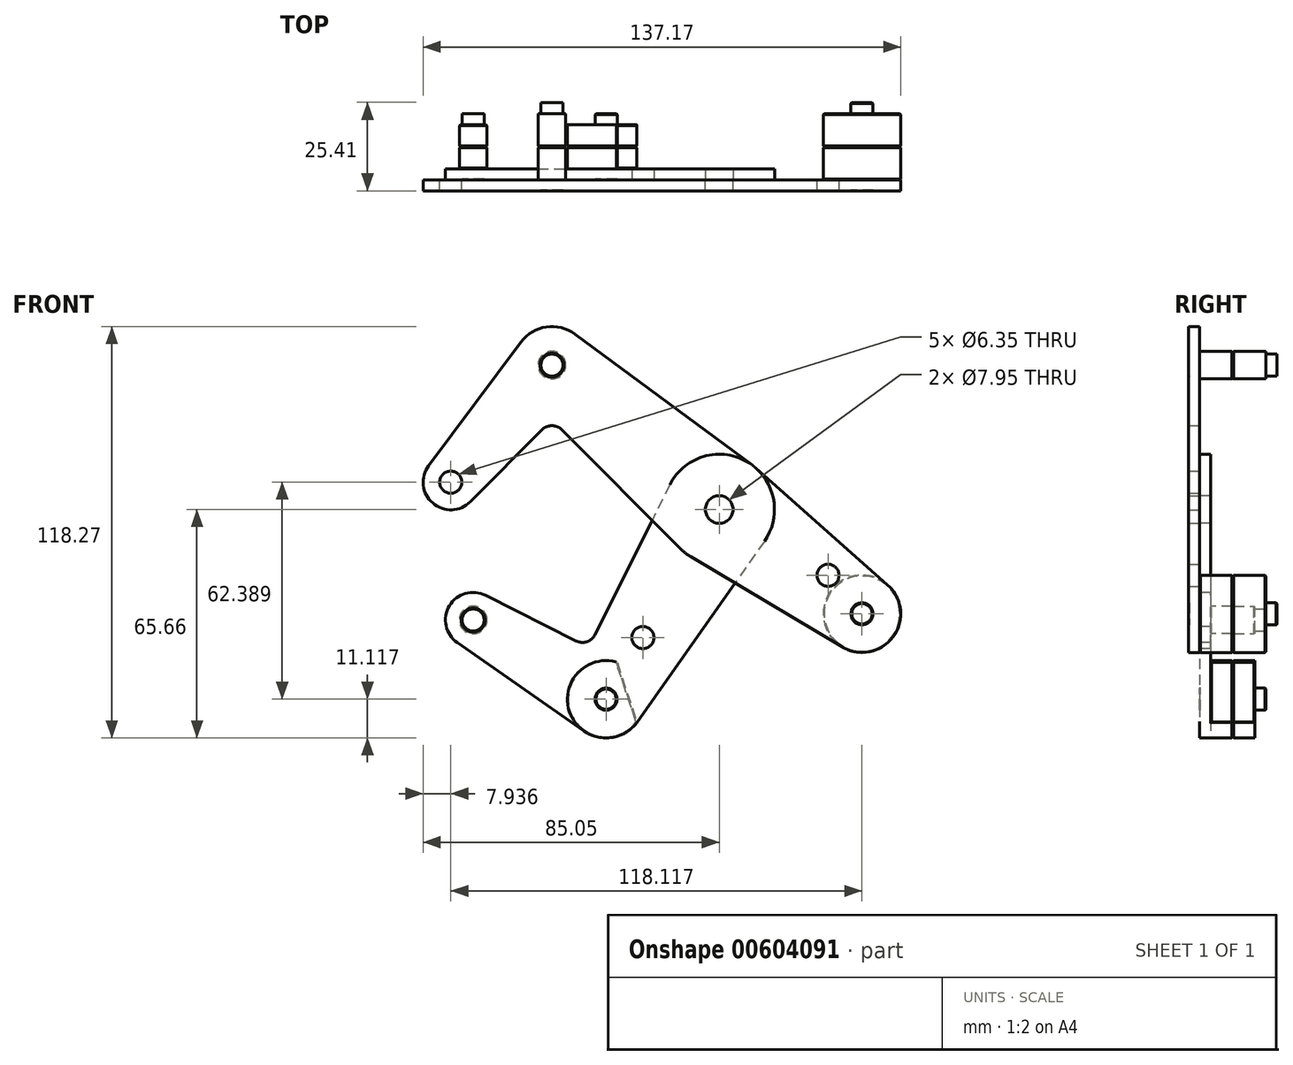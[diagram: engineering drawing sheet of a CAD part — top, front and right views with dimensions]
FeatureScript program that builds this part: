
annotation { "Feature Type Name" : "Feature", "Feature Type Description" : "" }
export const myFeature = defineFeature(function(context is Context, id is Id, definition is map)
    precondition{}
    {
        {
            var Q0;
            Q0=qCreatedBy(makeId("Front.planeOp"),FACE);
            var sketch = newSketch(context, id + "F0", { "sketchPlane" : qUnion([Q0])});
            skCircle(sketch, "E0", {"center": v(0, 0) * mm, "radius": 3.98 * mm});
            skCircle(sketch, "E1", {"center": v(0, 0) * mm, "radius": 15.88 * mm});
            skLineSegment(sketch, "E2", {"start": v(0, 0) * mm, "end": v(-48.07, 41.5) * mm, "construction": true});
            skLineSegment(sketch, "E3", {"start": v(-48.07, 41.5) * mm, "end": v(-77.11, 7.85) * mm, "construction": true});
            skCircle(sketch, "E4", {"center": v(-48.07, 41.5) * mm, "radius": 3.18 * mm});
            skCircle(sketch, "E5", {"center": v(-48.07, 41.5) * mm, "radius": 11.11 * mm});
            skCircle(sketch, "E6", {"center": v(-77.11, 7.85) * mm, "radius": 3.18 * mm});
            skCircle(sketch, "E7", {"center": v(-77.11, 7.85) * mm, "radius": 7.94 * mm});
            skLineSegment(sketch, "E8", {"start": v(0, 0) * mm, "end": v(41, -29.99) * mm, "construction": true});
            skCircle(sketch, "E9", {"center": v(41, -29.99) * mm, "radius": 3.18 * mm});
            skCircle(sketch, "E10", {"center": v(41, -29.99) * mm, "radius": 11.11 * mm});
            skCircle(sketch, "E11", {"center": v(31.24, -18.92) * mm, "radius": 3.18 * mm});
            skLineSegment(sketch, "E12", {"start": v(-83.48, 12.59) * mm, "end": v(-56.98, 48.14) * mm});
            skArc(sketch, "E13", {"start": v(-45.25, 22.92) * mm, "mid": v(-48.07, 24.1) * mm, "end": v(-50.88, 22.92) * mm});
            skLineSegment(sketch, "E14", {"start": v(-71.5, 2.24) * mm, "end": v(-50.88, 22.92) * mm});
            skLineSegment(sketch, "E15", {"start": v(-41.46, 50.43) * mm, "end": v(9.44, 12.76) * mm});
            skLineSegment(sketch, "E16", {"start": v(-45.25, 22.92) * mm, "end": v(-11.25, -11.2) * mm});
            skLineSegment(sketch, "E17", {"start": v(-8.13, -13.64) * mm, "end": v(35.31, -39.53) * mm});
            skLineSegment(sketch, "E18", {"start": v(10.53, 11.88) * mm, "end": v(48.38, -21.67) * mm});
            skLineSegment(sketch, "E19", {"start": v(0, 0) * mm, "end": v(-32.52, -54.54) * mm, "construction": true});
            skLineSegment(sketch, "E20", {"start": v(-32.52, -54.54) * mm, "end": v(-70.7, -31.78) * mm, "construction": true});
            skCircle(sketch, "E21", {"center": v(-32.52, -54.54) * mm, "radius": 3.18 * mm});
            skCircle(sketch, "E22", {"center": v(-32.52, -54.54) * mm, "radius": 11.11 * mm});
            skCircle(sketch, "E23", {"center": v(-70.7, -31.78) * mm, "radius": 3.18 * mm});
            skCircle(sketch, "E24", {"center": v(-70.7, -31.78) * mm, "radius": 7.94 * mm});
            skCircle(sketch, "E25", {"center": v(-21.94, -36.8) * mm, "radius": 3.18 * mm});
            skArc(sketch, "E26", {"start": v(-41.05, -37.81) * mm, "mid": v(-38, -38.03) * mm, "end": v(-35.7, -36.03) * mm});
            skLineSegment(sketch, "E27", {"start": v(12.99, -9.13) * mm, "end": v(-23.42, -60.93) * mm});
            skLineSegment(sketch, "E28", {"start": v(-14.2, 7.08) * mm, "end": v(-35.7, -36.03) * mm});
            skLineSegment(sketch, "E29", {"start": v(-67.13, -24.7) * mm, "end": v(-41.05, -37.81) * mm});
            skLineSegment(sketch, "E30", {"start": v(-75.24, -38.3) * mm, "end": v(-38.87, -63.66) * mm});
            skCircle(sketch, "E31", {"center": v(0, 0) * mm, "radius": 3.18 * mm});
            skSolve(sketch);
        }
        {
            var Q0;
            Q0=makeQuery(id+"F0.imprint","IMPRINT",FACE,{"disambiguationData":[TD([[makeQuery(id+"F0.imprint","IMPRINT",EDGE,{"derivedFrom":sQuery(id+"F0.wireOp",EDGE,"E4")}),-1.0]])]});
            var Q1;
            Q1=makeQuery(id+"F0.imprint","IMPRINT",FACE,{"disambiguationData":[TD([[makeQuery(id+"F0.imprint","IMPRINT",EDGE,{"derivedFrom":sQuery(id+"F0.wireOp",EDGE,"E6")}),-1.0]])]});
            var Q2;
            Q2=makeQuery(id+"F0.imprint","IMPRINT",FACE,{"disambiguationData":[TD([[makeQuery(id+"F0.imprint","IMPRINT",EDGE,{"derivedFrom":sQuery(id+"F0.wireOp",EDGE,"E9")}),-1.0]])]});
            var Q3;
            {var subQ0=sQuery(id+"F0.wireOp",EDGE,"E16");var subQ1=sQuery(id+"F0.wireOp",EDGE,"E1");var subQ2=makeQuery(id+"F0.imprint","INTERSECT",VERTEX,{"derivedFrom":[subQ1,subQ0]});Q3=makeQuery(id+"F0.imprint","IMPRINT",FACE,{"disambiguationData":[TD([[makeQuery(id+"F0.imprint","IMPRINT",EDGE,{"disambiguationData":[TD([[subQ2,1.0]])],"derivedFrom":subQ1}),-1.0]])]});}
            var Q4;
            {var subQ0=sQuery(id+"F0.wireOp",EDGE,"E17");var subQ1=sQuery(id+"F0.wireOp",EDGE,"E1");var subQ2=makeQuery(id+"F0.imprint","INTERSECT",VERTEX,{"derivedFrom":[subQ1,subQ0]});Q4=makeQuery(id+"F0.imprint","IMPRINT",FACE,{"disambiguationData":[TD([[makeQuery(id+"F0.imprint","IMPRINT",EDGE,{"disambiguationData":[TD([[subQ2,-1.0]])],"derivedFrom":subQ1}),-1.0]])]});}
            var Q5;
            {var subQ0=sQuery(id+"F0.wireOp",EDGE,"E12");Q5=makeQuery(id+"F0.imprint","IMPRINT",FACE,{"disambiguationData":[TD([[makeQuery(id+"F0.imprint","IMPRINT",EDGE,{"derivedFrom":subQ0}),-1.0]])]});}
            var Q6;
            Q6=makeQuery(id+"F0.imprint","IMPRINT",FACE,{"disambiguationData":[TD([[makeQuery(id+"F0.imprint","IMPRINT",EDGE,{"derivedFrom":sQuery(id+"F0.wireOp",EDGE,"E11")}),-1.0]])]});
            var Q7;
            Q7=makeQuery(id+"F0.imprint","IMPRINT",FACE,{"disambiguationData":[TD([[makeQuery(id+"F0.imprint","IMPRINT",EDGE,{"derivedFrom":sQuery(id+"F0.wireOp",EDGE,"E0")}),-1.0]])]});
            extrude(context, id + "F1", {"entities" : qUnion([Q0, Q1, Q2, Q3, Q4, Q5, Q6, Q7]), "depth" : 3.17 * mm, "offsetDistance" : 25.4 * mm});
        }
        {
            var Q0;
            Q0=makeQuery(id+"F0.imprint","IMPRINT",FACE,{"disambiguationData":[TD([[makeQuery(id+"F0.imprint","IMPRINT",EDGE,{"derivedFrom":sQuery(id+"F0.wireOp",EDGE,"E25")}),-1.0]])]});
            var Q1;
            Q1=makeQuery(id+"F0.imprint","IMPRINT",FACE,{"disambiguationData":[TD([[makeQuery(id+"F0.imprint","IMPRINT",EDGE,{"derivedFrom":sQuery(id+"F0.wireOp",EDGE,"E0")}),-1.0]])]});
            var Q2;
            {var subQ0=sQuery(id+"F0.wireOp",EDGE,"E17");var subQ1=sQuery(id+"F0.wireOp",EDGE,"E1");var subQ2=makeQuery(id+"F0.imprint","INTERSECT",VERTEX,{"derivedFrom":[subQ1,subQ0]});Q2=makeQuery(id+"F0.imprint","IMPRINT",FACE,{"disambiguationData":[TD([[makeQuery(id+"F0.imprint","IMPRINT",EDGE,{"disambiguationData":[TD([[subQ2,-1.0]])],"derivedFrom":subQ1}),-1.0]])]});}
            var Q3;
            {var subQ0=sQuery(id+"F0.wireOp",EDGE,"E16");var subQ1=sQuery(id+"F0.wireOp",EDGE,"E1");var subQ2=makeQuery(id+"F0.imprint","INTERSECT",VERTEX,{"derivedFrom":[subQ1,subQ0]});Q3=makeQuery(id+"F0.imprint","IMPRINT",FACE,{"disambiguationData":[TD([[makeQuery(id+"F0.imprint","IMPRINT",EDGE,{"disambiguationData":[TD([[subQ2,1.0]])],"derivedFrom":subQ1}),-1.0]])]});}
            var Q4;
            Q4=makeQuery(id+"F0.imprint","IMPRINT",FACE,{"disambiguationData":[TD([[makeQuery(id+"F0.imprint","IMPRINT",EDGE,{"derivedFrom":sQuery(id+"F0.wireOp",EDGE,"E23")}),-1.0]])]});
            var Q5;
            Q5=makeQuery(id+"F0.imprint","IMPRINT",FACE,{"disambiguationData":[TD([[makeQuery(id+"F0.imprint","IMPRINT",EDGE,{"derivedFrom":sQuery(id+"F0.wireOp",EDGE,"E21")}),-1.0]])]});
            extrude(context, id + "F2", {"entities" : qUnion([Q0, Q1, Q2, Q3, Q4, Q5]), "oppositeDirection" : true, "depth" : 3.17 * mm, "offsetDistance" : 25.4 * mm});
        }
        {
            var Q0;
            Q0=makeQuery(id+"F1.opExtrude","CAP_FACE",FACE,{"disambiguationData":[OSD([sQuery(id+"F0.wireOp",EDGE,"E0"),sQuery(id+"F0.wireOp",EDGE,"E1"),sQuery(id+"F0.wireOp",EDGE,"E4"),sQuery(id+"F0.wireOp",EDGE,"E5"),sQuery(id+"F0.wireOp",EDGE,"E6"),sQuery(id+"F0.wireOp",EDGE,"E7"),sQuery(id+"F0.wireOp",EDGE,"E9"),sQuery(id+"F0.wireOp",EDGE,"E10"),sQuery(id+"F0.wireOp",EDGE,"E11"),sQuery(id+"F0.wireOp",EDGE,"E12"),sQuery(id+"F0.wireOp",EDGE,"E13"),sQuery(id+"F0.wireOp",EDGE,"E14"),sQuery(id+"F0.wireOp",EDGE,"E15"),sQuery(id+"F0.wireOp",EDGE,"E16"),sQuery(id+"F0.wireOp",EDGE,"E17"),sQuery(id+"F0.wireOp",EDGE,"E18")])],"isStart":false});
            var sketch = newSketch(context, id + "F3", { "sketchPlane" : qUnion([Q0])});
            skCircle(sketch, "E32", {"center": v(41, -29.99) * mm, "radius": 11.11 * mm});
            skCircle(sketch, "E33", {"center": v(0, 0) * mm, "radius": 3.98 * mm});
            skCircle(sketch, "E34", {"center": v(-48.07, 41.5) * mm, "radius": 3.98 * mm});
            skSolve(sketch);
        }
        {
            var Q0;
            Q0=makeQuery(id+"F0.imprint","IMPRINT",FACE,{"disambiguationData":[TD([[makeQuery(id+"F0.imprint","IMPRINT",EDGE,{"derivedFrom":sQuery(id+"F0.wireOp",EDGE,"E25")}),-1.0]])]});
            var sketch = newSketch(context, id + "F4", { "sketchPlane" : qUnion([Q0])});
            skCircle(sketch, "E35", {"center": v(-32.52, -54.54) * mm, "radius": 11.11 * mm});
            skCircle(sketch, "E36", {"center": v(-70.7, -31.78) * mm, "radius": 3.98 * mm});
            skLineSegment(sketch, "E37", {"start": v(-29.38, -43.88) * mm, "end": v(-23.6, -61.18) * mm});
            skLineSegment(sketch, "E38", {"start": v(-26.5, -52.53) * mm, "end": v(41, -29.99) * mm, "construction": true});
            skSolve(sketch);
        }
        {
            var Q0;
            Q0=qCreatedBy(makeId("Front.planeOp"),FACE);
            cPlane(context, id + "F5", {"entities" : qUnion([Q0]), "cplaneType" : CPlaneType.OFFSET, "offset" : 9.52 * mm, "oppositeDirection" : true, "width" : 152.4 * mm, "height" : 152.4 * mm});
        }
        {
            var Q0;
            {var subQ2=sQuery(id+"F4.wireOp",EDGE,"E37");Q0=makeQuery(id+"F4.imprint","IMPRINT",FACE,{"disambiguationData":[TD([[makeQuery(id+"F4.imprint","IMPRINT",EDGE,{"derivedFrom":subQ2}),-1.0]])]});}
            var Q1;
            Q1=makeQuery(id+"F3.imprint","IMPRINT",FACE,{"disambiguationData":[TD([[makeQuery(id+"F3.imprint","IMPRINT",EDGE,{"derivedFrom":makeQuery(id+"F1.opExtrude","CAP_EDGE",EDGE,{"disambiguationData":[OSD([sQuery(id+"F0.wireOp",EDGE,"E9")])],"isStart":false})}),1.0]])]});
            var Q2;
            Q2=makeQuery(id+"F3.imprint","IMPRINT",FACE,{"disambiguationData":[TD([[makeQuery(id+"F3.imprint","IMPRINT",EDGE,{"derivedFrom":makeQuery(id+"F1.opExtrude","CAP_EDGE",EDGE,{"disambiguationData":[OSD([sQuery(id+"F0.wireOp",EDGE,"E9")])],"isStart":false})}),-1.0]])]});
            var Q3;
            Q3=makeQuery(id+"F3.imprint","IMPRINT",FACE,{"disambiguationData":[TD([[makeQuery(id+"F3.imprint","IMPRINT",EDGE,{"derivedFrom":makeQuery(id+"F1.opExtrude","CAP_EDGE",EDGE,{"disambiguationData":[OSD([sQuery(id+"F0.wireOp",EDGE,"E4")])],"isStart":false})}),1.0]])]});
            var Q4;
            Q4=makeQuery(id+"F4.imprint","IMPRINT",FACE,{"disambiguationData":[TD([[makeQuery(id+"F4.imprint","IMPRINT",EDGE,{"derivedFrom":sQuery(id+"F4.wireOp",EDGE,"E36")}),1.0]])]});
            var Q5;
            Q5=makeQuery(id+"F3.imprint","IMPRINT",FACE,{"disambiguationData":[TD([[makeQuery(id+"F3.imprint","IMPRINT",EDGE,{"derivedFrom":sQuery(id+"F3.wireOp",EDGE,"E34")}),1.0]])]});
            var Q6;
            Q6=qCreatedBy(id+"F5.planeOp",FACE);
            extrude(context, id + "F6", {"entities" : qUnion([Q0, Q1, Q2, Q3, Q4, Q5]), "endBound" : BoundingType.UP_TO_SURFACE, "oppositeDirection" : true, "depth" : 25.4 * mm, "endBoundEntityFace" : qUnion([Q6]), "offsetDistance" : 25.4 * mm});
        }
        {
            var Q0;
            Q0=makeQuery(id+"F1.opExtrude","SWEPT_BODY",BODY,{"disambiguationData":[OSD([sQuery(id+"F0.wireOp",EDGE,"E0"),sQuery(id+"F0.wireOp",EDGE,"E1"),sQuery(id+"F0.wireOp",EDGE,"E4"),sQuery(id+"F0.wireOp",EDGE,"E5"),sQuery(id+"F0.wireOp",EDGE,"E6"),sQuery(id+"F0.wireOp",EDGE,"E7"),sQuery(id+"F0.wireOp",EDGE,"E9"),sQuery(id+"F0.wireOp",EDGE,"E10"),sQuery(id+"F0.wireOp",EDGE,"E11"),sQuery(id+"F0.wireOp",EDGE,"E12"),sQuery(id+"F0.wireOp",EDGE,"E13"),sQuery(id+"F0.wireOp",EDGE,"E14"),sQuery(id+"F0.wireOp",EDGE,"E15"),sQuery(id+"F0.wireOp",EDGE,"E16"),sQuery(id+"F0.wireOp",EDGE,"E17"),sQuery(id+"F0.wireOp",EDGE,"E18")])]});
            var Q1;
            Q1=makeQuery(id+"F2.opExtrude","SWEPT_BODY",BODY,{"disambiguationData":[OSD([sQuery(id+"F0.wireOp",EDGE,"E0"),sQuery(id+"F0.wireOp",EDGE,"E1"),sQuery(id+"F0.wireOp",EDGE,"E21"),sQuery(id+"F0.wireOp",EDGE,"E22"),sQuery(id+"F0.wireOp",EDGE,"E23"),sQuery(id+"F0.wireOp",EDGE,"E24"),sQuery(id+"F0.wireOp",EDGE,"E25"),sQuery(id+"F0.wireOp",EDGE,"E26"),sQuery(id+"F0.wireOp",EDGE,"E27"),sQuery(id+"F0.wireOp",EDGE,"E28"),sQuery(id+"F0.wireOp",EDGE,"E29"),sQuery(id+"F0.wireOp",EDGE,"E30")])]});
            var Q2;
            Q2=makeQuery(id+"F6.opExtrude","SWEPT_BODY",BODY,{"disambiguationData":[OSD([sQuery(id+"F3.wireOp",EDGE,"E34")])]});
            var Q3;
            Q3=makeQuery(id+"F6.opExtrude","SWEPT_BODY",BODY,{"disambiguationData":[OSD([sQuery(id+"F3.wireOp",EDGE,"E32")])]});
            var Q4;
            Q4=makeQuery(id+"F6.opExtrude","SWEPT_BODY",BODY,{"disambiguationData":[OSD([sQuery(id+"F4.wireOp",EDGE,"E35"),sQuery(id+"F4.wireOp",EDGE,"E37")])]});
            var Q5;
            Q5=makeQuery(id+"F6.opExtrude","SWEPT_BODY",BODY,{"disambiguationData":[OSD([sQuery(id+"F4.wireOp",EDGE,"E36")])]});
            booleanBodies(context, id + "F7", {"operationType" : BooleanOperationType.SUBTRACTION, "tools" : qUnion([Q0, Q1]), "targets" : qUnion([Q2, Q3, Q4, Q5]), "keepTools" : true});
        }
        {
            var Q0;
            Q0=makeQuery(id+"F6.opExtrude","CAP_FACE",FACE,{"disambiguationData":[OSD([sQuery(id+"F3.wireOp",EDGE,"E32")])],"isStart":false});
            var Q1;
            Q1=makeQuery(id+"F6.opExtrude","SWEPT_FACE",FACE,{"disambiguationData":[OSD([sQuery(id+"F3.wireOp",EDGE,"E32")])]});
            var Q2;
            Q2=makeQuery(id+"F6.opExtrude","SWEPT_FACE",FACE,{"disambiguationData":[OSD([sQuery(id+"F4.wireOp",EDGE,"E37")])]});
            var Q3;
            Q3=makeQuery(id+"F6.opExtrude","CAP_FACE",FACE,{"disambiguationData":[OSD([sQuery(id+"F4.wireOp",EDGE,"E35"),sQuery(id+"F4.wireOp",EDGE,"E37")])],"isStart":false});
            var Q4;
            Q4=makeQuery(id+"F6.opExtrude","CAP_EDGE",EDGE,{"disambiguationData":[OSD([sQuery(id+"F4.wireOp",EDGE,"E36")])],"isStart":false});
            var Q5;
            Q5=makeQuery(id+"F6.opExtrude","SWEPT_FACE",FACE,{"disambiguationData":[OSD([sQuery(id+"F4.wireOp",EDGE,"E36")])]});
            var Q6;
            Q6=makeQuery(id+"F6.opExtrude","CAP_FACE",FACE,{"disambiguationData":[OSD([sQuery(id+"F3.wireOp",EDGE,"E34")])],"isStart":false});
            var Q7;
            Q7=makeQuery(id+"F6.opExtrude","SWEPT_FACE",FACE,{"disambiguationData":[OSD([sQuery(id+"F0.wireOp",EDGE,"E4")])]});
            var Q8;
            Q8=makeQuery(id+"F6.opExtrude","CAP_FACE",FACE,{"disambiguationData":[OSD([sQuery(id+"F3.wireOp",EDGE,"E32")])],"isStart":true});
            var Q9;
            Q9=makeQuery(id+"F6.opExtrude","CAP_FACE",FACE,{"disambiguationData":[OSD([sQuery(id+"F4.wireOp",EDGE,"E35"),sQuery(id+"F4.wireOp",EDGE,"E37")])],"isStart":true});
            var Q10;
            Q10=makeQuery(id+"F2.opExtrude","CAP_EDGE",EDGE,{"disambiguationData":[OSD([sQuery(id+"F0.wireOp",EDGE,"E23")])],"isStart":true});
            var Q11;
            Q11=makeQuery(id+"F1.opExtrude","CAP_EDGE",EDGE,{"disambiguationData":[OSD([sQuery(id+"F0.wireOp",EDGE,"E4")])],"isStart":false});
            chamfer(context, id + "F8", {"entities" : qUnion([Q0, Q1, Q2, Q3, Q4, Q5, Q6, Q7, Q8, Q9, Q10, Q11]), "width" : 0.25 * mm, "tangentPropagation" : true});
        }
        {
            var Q0;
            Q0=makeQuery(id+"F6.opExtrude","SWEPT_BODY",BODY,{"disambiguationData":[OSD([sQuery(id+"F3.wireOp",EDGE,"E34")])]});
            var Q1;
            Q1=makeQuery(id+"F6.opExtrude","SWEPT_BODY",BODY,{"disambiguationData":[OSD([sQuery(id+"F3.wireOp",EDGE,"E32")])]});
            var Q2;
            Q2=makeQuery(id+"F6.opExtrude","SWEPT_BODY",BODY,{"disambiguationData":[OSD([sQuery(id+"F4.wireOp",EDGE,"E35"),sQuery(id+"F4.wireOp",EDGE,"E37")])]});
            var Q3;
            Q3=makeQuery(id+"F6.opExtrude","SWEPT_BODY",BODY,{"disambiguationData":[OSD([sQuery(id+"F4.wireOp",EDGE,"E36")])]});
            var Q4;
            Q4=qCreatedBy(id+"F5.planeOp",FACE);
            mirror(context, id + "F9", {"operationType" : NewBodyOperationType.ADD, "entities" : qUnion([Q0, Q1, Q2, Q3]), "mirrorPlane" : qUnion([Q4])});
        }
    });
